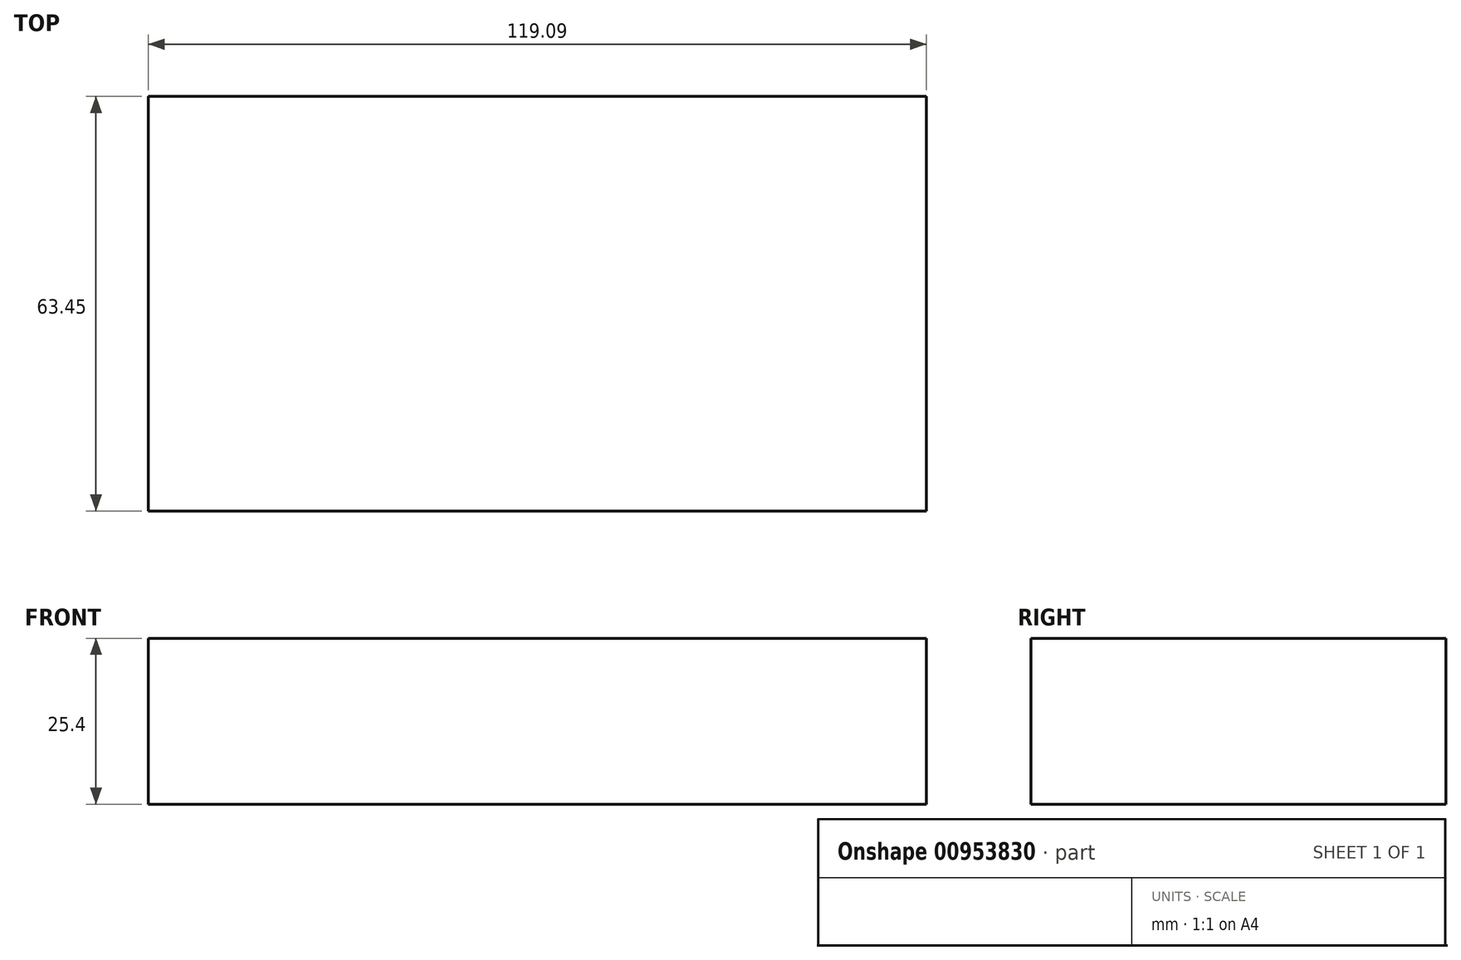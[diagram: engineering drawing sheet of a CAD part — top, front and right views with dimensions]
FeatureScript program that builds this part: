
annotation { "Feature Type Name" : "Feature", "Feature Type Description" : "" }
export const myFeature = defineFeature(function(context is Context, id is Id, definition is map)
    precondition{}
    {
        {
            var Q0;
            Q0=qCreatedBy(makeId("Top.planeOp"),FACE);
            var sketch = newSketch(context, id + "F0", { "sketchPlane" : qUnion([Q0])});
            skLineSegment(sketch, "E0.bottom", {"start": v(0, 0) * mm, "end": v(-119.1, 0) * mm});
            skLineSegment(sketch, "E0.top", {"start": v(0, 63.45) * mm, "end": v(-119.1, 63.45) * mm});
            skLineSegment(sketch, "E0.left", {"start": v(0, 0) * mm, "end": v(0, 63.45) * mm});
            skLineSegment(sketch, "E0.right", {"start": v(-119.1, 0) * mm, "end": v(-119.1, 63.45) * mm});
            skSolve(sketch);
        }
        {
            var Q0;
            Q0=makeQuery(id+"F0.imprint","IMPRINT",FACE,{"disambiguationData":[TD([[makeQuery(id+"F0.imprint","IMPRINT",EDGE,{"derivedFrom":sQuery(id+"F0.wireOp",EDGE,"E0.bottom")}),-1.0]])]});
            extrude(context, id + "F1", {"entities" : qUnion([Q0]), "depth" : 25.4 * mm, "offsetDistance" : 25.4 * mm});
        }
    });
